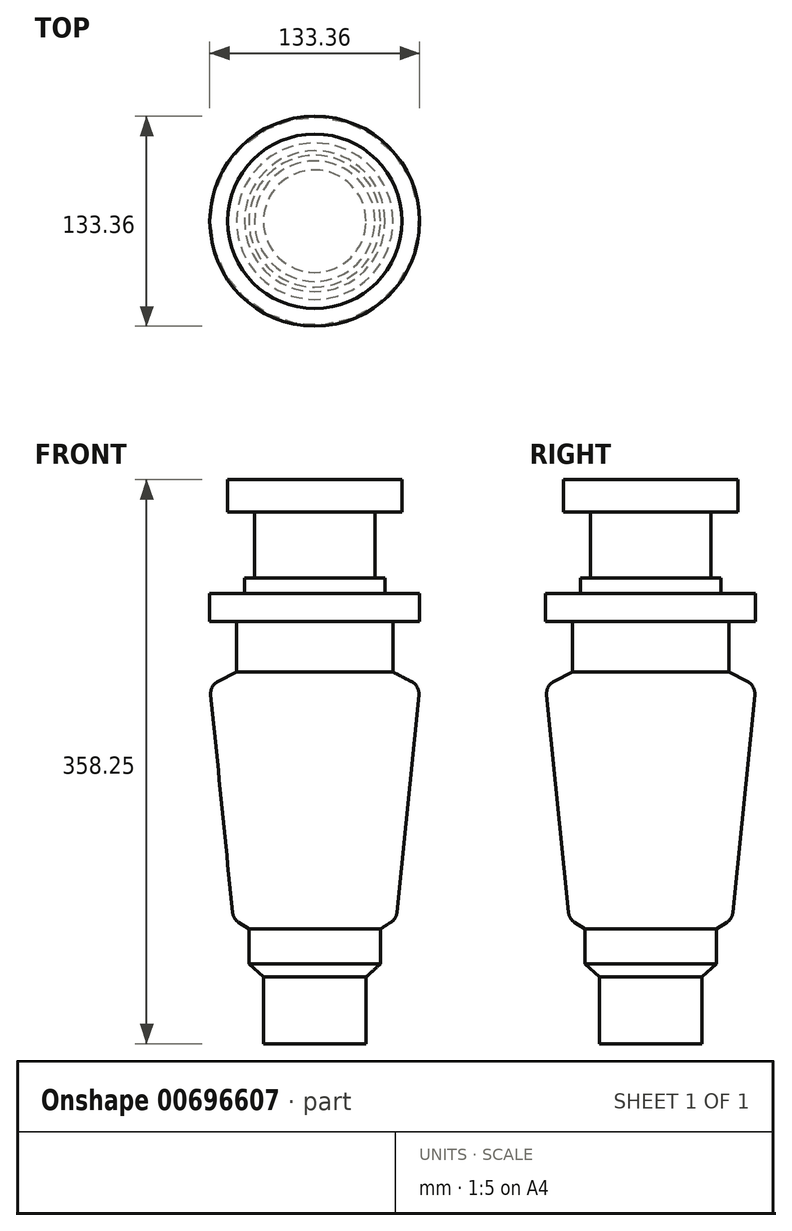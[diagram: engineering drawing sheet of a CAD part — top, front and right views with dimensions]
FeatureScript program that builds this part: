
annotation { "Feature Type Name" : "Feature", "Feature Type Description" : "" }
export const myFeature = defineFeature(function(context is Context, id is Id, definition is map)
    precondition{}
    {
        {
            var Q0;
            Q0=qCreatedBy(makeId("Front.planeOp"),FACE);
            var sketch = newSketch(context, id + "F0", { "sketchPlane" : qUnion([Q0])});
            skSolve(sketch);
        }
        {
            var Q0;
            Q0=qCreatedBy(makeId("Front.planeOp"),FACE);
            var sketch = newSketch(context, id + "F1", { "sketchPlane" : qUnion([Q0])});
            skLineSegment(sketch, "E0", {"start": v(0, 358.25) * mm, "end": v(0, 0) * mm});
            skLineSegment(sketch, "E1", {"start": v(0, 0) * mm, "end": v(-32.56, 0) * mm});
            skLineSegment(sketch, "E2", {"start": v(-32.56, 0) * mm, "end": v(-32.56, 42.28) * mm});
            skLineSegment(sketch, "E3", {"start": v(-32.56, 42.28) * mm, "end": v(-41.82, 50.83) * mm});
            skLineSegment(sketch, "E4", {"start": v(-41.82, 50.83) * mm, "end": v(-41.82, 72.9) * mm});
            skLineSegment(sketch, "E5", {"start": v(-41.82, 72.9) * mm, "end": v(-51.8, 79.32) * mm});
            skLineSegment(sketch, "E6", {"start": v(-51.8, 79.32) * mm, "end": v(-66.68, 227.3) * mm});
            skLineSegment(sketch, "E7", {"start": v(-66.68, 227.3) * mm, "end": v(-49.66, 236) * mm});
            skLineSegment(sketch, "E8", {"start": v(-49.66, 236) * mm, "end": v(-49.66, 268.01) * mm});
            skLineSegment(sketch, "E9", {"start": v(-49.66, 268.01) * mm, "end": v(-66.68, 268.01) * mm});
            skLineSegment(sketch, "E10", {"start": v(-66.68, 268.01) * mm, "end": v(-66.68, 285.86) * mm});
            skLineSegment(sketch, "E11", {"start": v(-66.68, 285.86) * mm, "end": v(-44.67, 285.86) * mm});
            skLineSegment(sketch, "E12", {"start": v(-44.67, 285.86) * mm, "end": v(-44.67, 295.83) * mm});
            skLineSegment(sketch, "E13", {"start": v(-44.67, 295.83) * mm, "end": v(-38.26, 295.83) * mm});
            skLineSegment(sketch, "E14", {"start": v(-38.26, 295.83) * mm, "end": v(-38.26, 337.86) * mm});
            skLineSegment(sketch, "E15", {"start": v(-38.26, 337.86) * mm, "end": v(-55.4, 337.86) * mm});
            skLineSegment(sketch, "E16", {"start": v(-55.4, 337.86) * mm, "end": v(-55.4, 358.25) * mm});
            skLineSegment(sketch, "E17", {"start": v(-55.4, 358.25) * mm, "end": v(0, 358.25) * mm});
            skSolve(sketch);
        }
        {
            var Q0;
            Q0 = qSketchRegion(id + "F1", true);
            var Q1;
            Q1=sQuery(id+"F1.wireOp",EDGE,"E0");
            revolve(context, id + "F2", {"entities" : qUnion([Q0]), "axis" : qUnion([Q1]), "revolveType" : RevolveType.FULL});
        }
        {
            var Q0;
            Q0=makeQuery(id+"F2.opRevolve","SWEPT_EDGE",EDGE,{"disambiguationData":[OSD([sQuery(id+"F1.wireOp",EDGE,"E6"),sQuery(id+"F1.wireOp",EDGE,"E7")])]});
            var Q1;
            Q1=makeQuery(id+"F2.opRevolve","SWEPT_EDGE",EDGE,{"disambiguationData":[OSD([sQuery(id+"F1.wireOp",EDGE,"E5"),sQuery(id+"F1.wireOp",EDGE,"E6")])]});
            fillet(context, id + "F3", {"entities" : qUnion([Q0, Q1]), "radius" : 8.43 * mm, "tangentPropagation" : true, "allowEdgeOverflow" : false});
        }
    });
